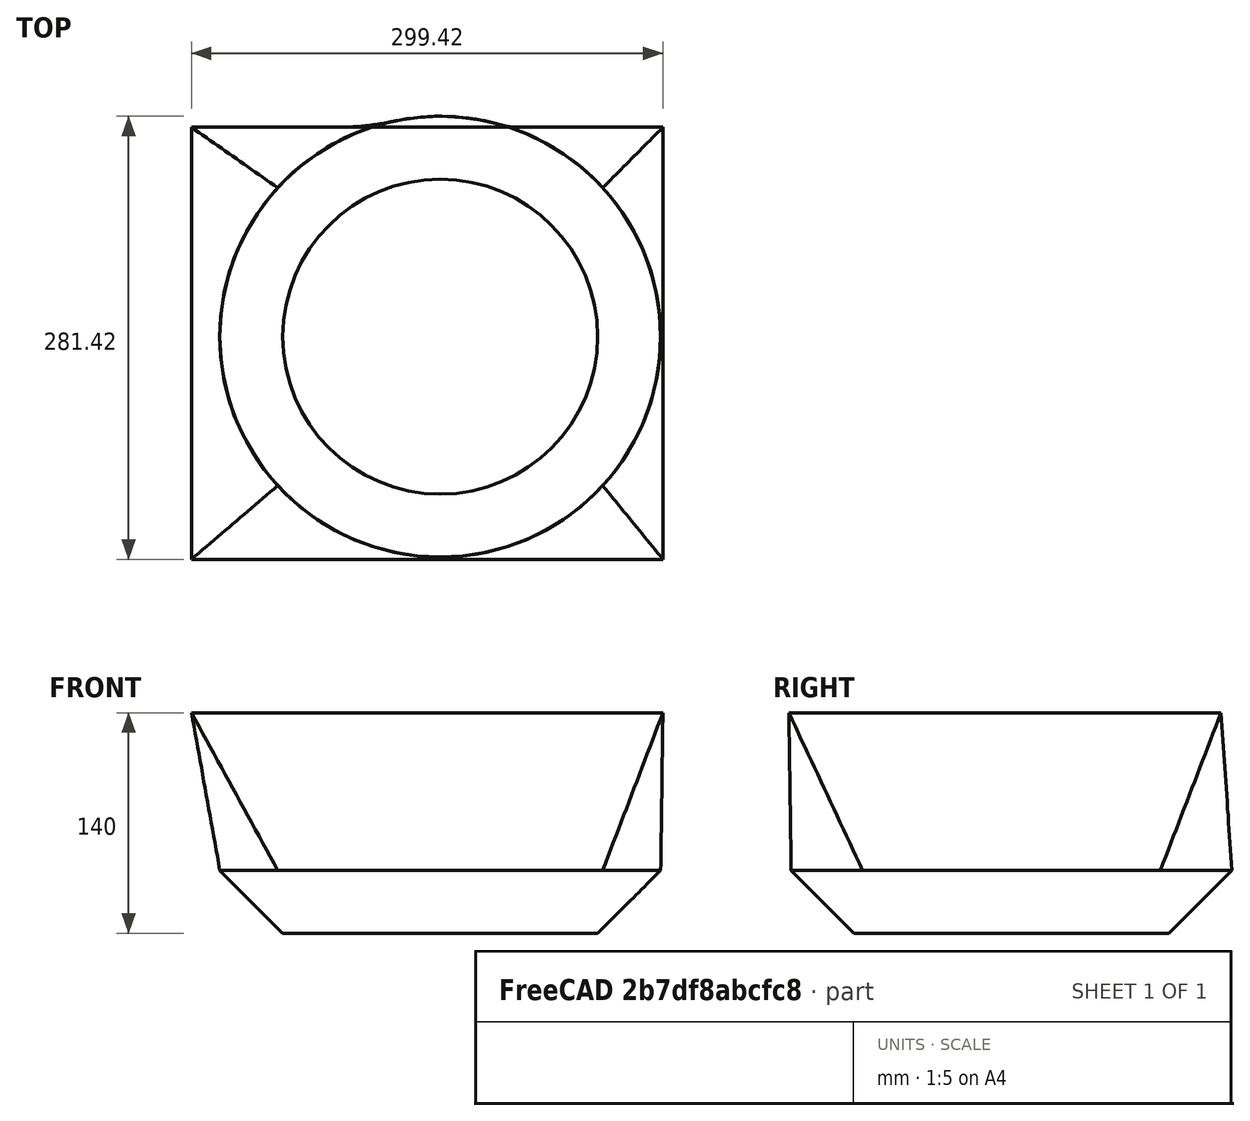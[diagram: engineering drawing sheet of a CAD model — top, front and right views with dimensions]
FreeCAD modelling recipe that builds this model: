
FCSTD DOCUMENT  (FreeCAD 0.15R4671 (Git))
Label: mark1
License: All rights reserved
LicenseURL: http://en.wikipedia.org/wiki/All_rights_reserved
objects: Part::Part2DObjectPython×3, Part::Loft×2
note: 5 computed .brp shape members not serialized (recipe doc carries the construction recipe); baked Part::Feature solids carry a one-line shape summary decoded from their .brp

FEATURE [Part::Part2DObjectPython] Circle  # Draft 2D object (typed FeaturePython)
  FirstAngle = 0
  LastAngle = 0
  MakeFace = true
  Radius = 140
FEATURE [Part::Part2DObjectPython] Rectangle  # Draft 2D object (typed FeaturePython)
  ChamferSize = 0
  FilletRadius = 0
  Height = 274.421
  Length = -299.421
  MakeFace = true
  Placement = pos=(141.421,-141.421,100) rot=(0,0,1;0rad)
FEATURE [Part::Part2DObjectPython] Circle001  # Draft 2D object (typed FeaturePython)
  FirstAngle = 0
  LastAngle = 0
  MakeFace = true
  Placement = pos=(0,0,-40) rot=(0,0,1;0rad)
  Radius = 100
FEATURE [Part::Loft] Loft
  Closed = false
  Ruled = false
  Sections = -> [Circle001,Circle]
  Solid = false
FEATURE [Part::Loft] Loft001
  Closed = false
  Ruled = false
  Sections = -> [Rectangle,Circle]
  Solid = false
